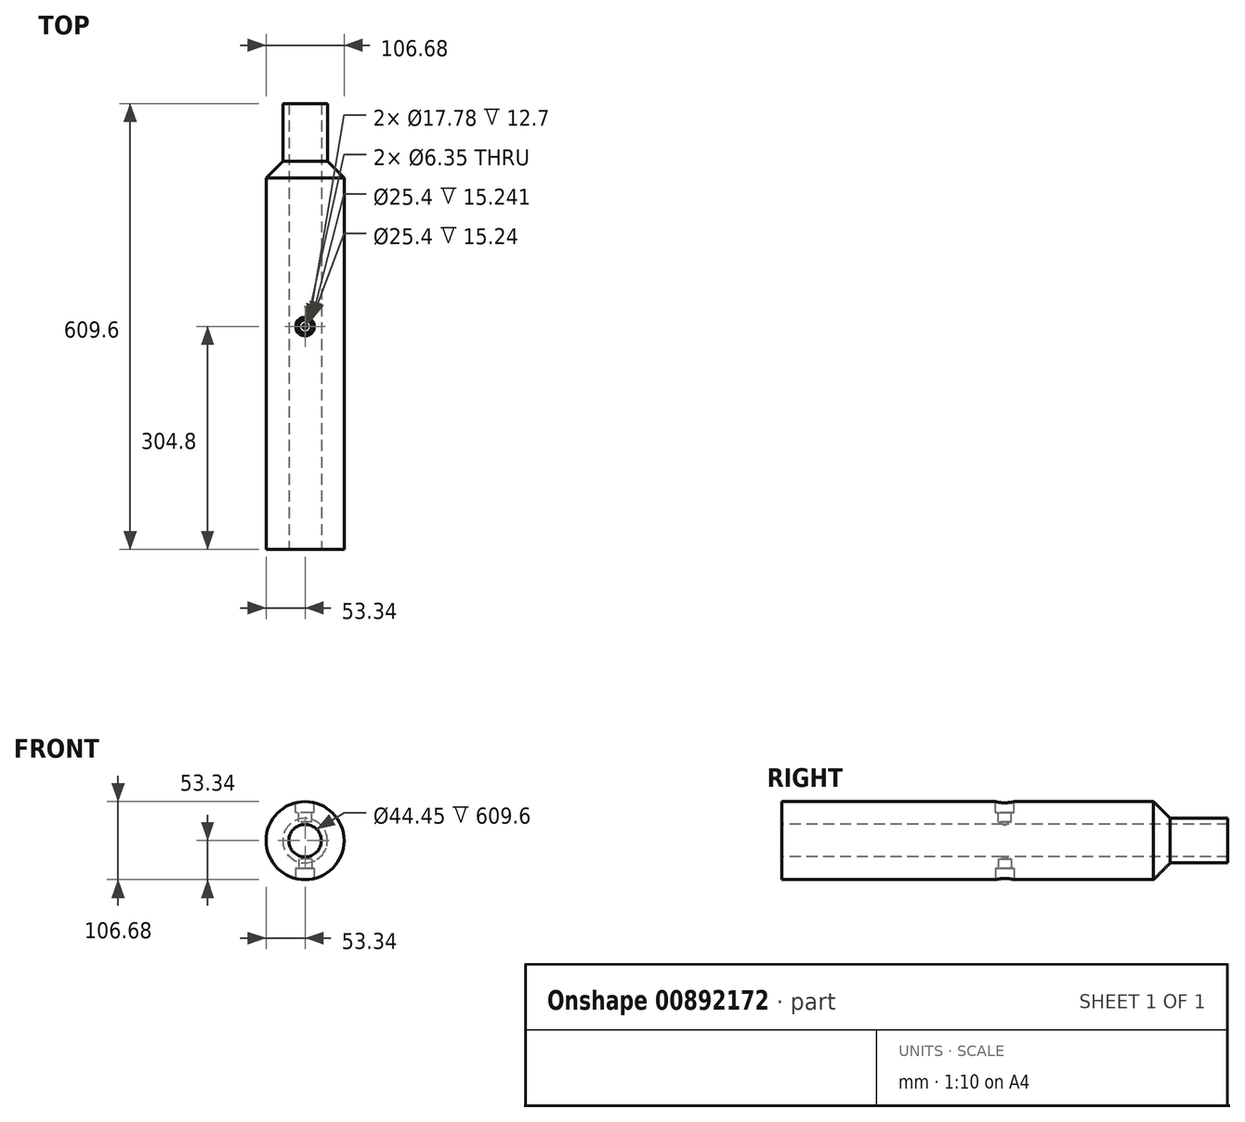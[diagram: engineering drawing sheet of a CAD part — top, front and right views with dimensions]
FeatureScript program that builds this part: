
annotation { "Feature Type Name" : "Feature", "Feature Type Description" : "" }
export const myFeature = defineFeature(function(context is Context, id is Id, definition is map)
    precondition{}
    {
        {
            var Q0;
            Q0=qCreatedBy(makeId("Front.planeOp"),FACE);
            var sketch = newSketch(context, id + "F0", { "sketchPlane" : qUnion([Q0])});
            skCircle(sketch, "E0", {"center": v(0, 0) * mm, "radius": 22.23 * mm});
            skCircle(sketch, "E1", {"center": v(0, 0) * mm, "radius": 53.34 * mm});
            skSolve(sketch);
        }
        {
            var Q0;
            Q0=makeQuery(id+"F0.imprint","IMPRINT",FACE,{"disambiguationData":[TD([[makeQuery(id+"F0.imprint","IMPRINT",EDGE,{"derivedFrom":sQuery(id+"F0.wireOp",EDGE,"E0")}),-1.0]])]});
            extrude(context, id + "F1", {"entities" : qUnion([Q0]), "endBound" : BoundingType.SYMMETRIC, "oppositeDirection" : true, "depth" : 609.6 * mm, "offsetDistance" : 25.4 * mm});
        }
        {
            var Q0;
            Q0=makeQuery(id+"F1.opExtrude","CAP_FACE",FACE,{"disambiguationData":[OSD([sQuery(id+"F0.wireOp",EDGE,"E0"),sQuery(id+"F0.wireOp",EDGE,"E1")])],"isStart":false});
            cPlane(context, id + "F2", {"entities" : qUnion([Q0]), "cplaneType" : CPlaneType.OFFSET, "offset" : 0 * mm, "oppositeDirection" : true, "width" : 152.4 * mm, "height" : 152.4 * mm});
        }
        {
            var Q0;
            Q0=qCreatedBy(makeId("Front.planeOp"),FACE);
            cPlane(context, id + "F3", {"entities" : qUnion([Q0]), "cplaneType" : CPlaneType.OFFSET, "offset" : 203.2 * mm, "oppositeDirection" : true, "width" : 152.4 * mm, "height" : 152.4 * mm});
        }
        {
            var Q0;
            Q0=qCreatedBy(id+"F2.planeOp",FACE);
            var sketch = newSketch(context, id + "F4", { "sketchPlane" : qUnion([Q0])});
            skCircle(sketch, "E2", {"center": v(0, 0) * mm, "radius": 22.23 * mm});
            skCircle(sketch, "E3", {"center": v(0, 0) * mm, "radius": 30.48 * mm});
            skCircle(sketch, "E4", {"center": v(0, 0) * mm, "radius": 53.34 * mm});
            skSolve(sketch);
        }
        {
            var Q0;
            Q0=makeQuery(id+"F4.imprint","IMPRINT",FACE,{"disambiguationData":[TD([[makeQuery(id+"F4.imprint","IMPRINT",EDGE,{"derivedFrom":sQuery(id+"F4.wireOp",EDGE,"E3")}),-1.0]])]});
            var Q1;
            Q1=qCreatedBy(id+"F3.planeOp",FACE);
            extrude(context, id + "F5", {"entities" : qUnion([Q0]), "operationType" : NewBodyOperationType.REMOVE, "oppositeDirection" : true, "depth" : 101.6 * mm, "endBoundEntityFace" : qUnion([Q1]), "offsetDistance" : 25.4 * mm});
        }
        {
            var Q0;
            Q0=qCreatedBy(makeId("Right.planeOp"),FACE);
            var sketch = newSketch(context, id + "F6", { "sketchPlane" : qUnion([Q0])});
            skLineSegment(sketch, "E5", {"start": v(0, 0) * mm, "end": v(203.2, 0) * mm, "construction": true});
            skLineSegment(sketch, "E6", {"start": v(203.2, 0) * mm, "end": v(203.2, 53.34) * mm});
            skLineSegment(sketch, "E7", {"start": v(203.2, 0) * mm, "end": v(203.2, 30.48) * mm});
            skLineSegment(sketch, "E8", {"start": v(203.2, 30.48) * mm, "end": v(226.06, 30.48) * mm});
            skLineSegment(sketch, "E9", {"start": v(226.06, 30.48) * mm, "end": v(203.2, 53.34) * mm});
            skSolve(sketch);
        }
        {
            var Q0;
            Q0=makeQuery(id+"F6.imprint","IMPRINT",FACE,{"disambiguationData":[TD([[makeQuery(id+"F6.imprint","IMPRINT",EDGE,{"derivedFrom":sQuery(id+"F6.wireOp",EDGE,"E6")}),-1.0]])]});
            var Q1;
            Q1=sQuery(id+"F6.wireOp",EDGE,"E5");
            revolve(context, id + "F7", {"operationType" : NewBodyOperationType.ADD, "surfaceOperationType" : NewSurfaceOperationType.NEW, "entities" : qUnion([Q0]), "axis" : qUnion([Q1]), "revolveType" : RevolveType.FULL});
        }
        {
            var Q0;
            Q0=qCreatedBy(makeId("Top.planeOp"),FACE);
            cPlane(context, id + "F8", {"entities" : qUnion([Q0]), "cplaneType" : CPlaneType.OFFSET, "offset" : 53.34 * mm, "width" : 152.4 * mm, "height" : 152.4 * mm});
        }
        {
            var Q0;
            Q0=qCreatedBy(makeId("Top.planeOp"),FACE);
            cPlane(context, id + "F9", {"entities" : qUnion([Q0]), "cplaneType" : CPlaneType.OFFSET, "offset" : 53.34 * mm, "oppositeDirection" : true, "width" : 152.4 * mm, "height" : 152.4 * mm});
        }
        {
            var Q0;
            Q0=qCreatedBy(id+"F8.planeOp",FACE);
            var sketch = newSketch(context, id + "F10", { "sketchPlane" : qUnion([Q0])});
            skCircle(sketch, "E10", {"center": v(0, 0) * mm, "radius": 12.7 * mm});
            skCircle(sketch, "E11", {"center": v(0, 0) * mm, "radius": 8.9 * mm});
            skCircle(sketch, "E12", {"center": v(0, 0) * mm, "radius": 3.18 * mm});
            skSolve(sketch);
        }
        {
            var Q0;
            Q0=makeQuery(id+"F10.imprint","IMPRINT",FACE,{"disambiguationData":[TD([[makeQuery(id+"F10.imprint","IMPRINT",EDGE,{"derivedFrom":sQuery(id+"F10.wireOp",EDGE,"E10")}),1.0]])]});
            var Q1;
            Q1=makeQuery(id+"F10.imprint","IMPRINT",FACE,{"disambiguationData":[TD([[makeQuery(id+"F10.imprint","IMPRINT",EDGE,{"derivedFrom":sQuery(id+"F10.wireOp",EDGE,"E12")}),1.0]])]});
            var Q2;
            Q2=makeQuery(id+"F10.imprint","IMPRINT",FACE,{"disambiguationData":[TD([[makeQuery(id+"F10.imprint","IMPRINT",EDGE,{"derivedFrom":sQuery(id+"F10.wireOp",EDGE,"E11")}),1.0]])]});
            extrude(context, id + "F11", {"entities" : qUnion([Q0, Q1, Q2]), "operationType" : NewBodyOperationType.REMOVE, "oppositeDirection" : true, "depth" : 15.24 * mm, "offsetDistance" : 25.4 * mm});
        }
        {
            var Q0;
            Q0=makeQuery(id+"F10.imprint","IMPRINT",FACE,{"disambiguationData":[TD([[makeQuery(id+"F10.imprint","IMPRINT",EDGE,{"derivedFrom":sQuery(id+"F10.wireOp",EDGE,"E11")}),1.0]])]});
            var Q1;
            Q1=makeQuery(id+"F10.imprint","IMPRINT",FACE,{"disambiguationData":[TD([[makeQuery(id+"F10.imprint","IMPRINT",EDGE,{"derivedFrom":sQuery(id+"F10.wireOp",EDGE,"E12")}),1.0]])]});
            extrude(context, id + "F12", {"entities" : qUnion([Q0, Q1]), "operationType" : NewBodyOperationType.REMOVE, "oppositeDirection" : true, "depth" : 27.94 * mm, "offsetDistance" : 25.4 * mm});
        }
        {
            var Q0;
            Q0=makeQuery(id+"F10.imprint","IMPRINT",FACE,{"disambiguationData":[TD([[makeQuery(id+"F10.imprint","IMPRINT",EDGE,{"derivedFrom":sQuery(id+"F10.wireOp",EDGE,"E12")}),1.0]])]});
            var Q1;
            Q1=makeQuery(id+"F1.opExtrude","SWEPT_FACE",FACE,{"disambiguationData":[OSD([sQuery(id+"F0.wireOp",EDGE,"E0")])]});
            extrude(context, id + "F13", {"entities" : qUnion([Q0]), "operationType" : NewBodyOperationType.REMOVE, "endBound" : BoundingType.UP_TO_SURFACE, "oppositeDirection" : true, "depth" : 53.34 * mm, "endBoundEntityFace" : qUnion([Q1]), "offsetDistance" : 25.4 * mm});
        }
        {
            var Q0;
            Q0=qCreatedBy(id+"F9.planeOp",FACE);
            var sketch = newSketch(context, id + "F14", { "sketchPlane" : qUnion([Q0])});
            skCircle(sketch, "E13", {"center": v(0, 0) * mm, "radius": 12.7 * mm});
            skCircle(sketch, "E14", {"center": v(0, 0) * mm, "radius": 8.9 * mm});
            skCircle(sketch, "E15", {"center": v(0, 0) * mm, "radius": 3.18 * mm});
            skSolve(sketch);
        }
        {
            var Q0;
            Q0 = qSketchRegion(id + "F14", true);
            var Q1;
            Q1=makeQuery(id+"F14.imprint","IMPRINT",FACE,{"disambiguationData":[TD([[makeQuery(id+"F14.imprint","IMPRINT",EDGE,{"derivedFrom":sQuery(id+"F14.wireOp",EDGE,"E14")}),1.0]])]});
            var Q2;
            Q2=makeQuery(id+"F14.imprint","IMPRINT",FACE,{"disambiguationData":[TD([[makeQuery(id+"F14.imprint","IMPRINT",EDGE,{"derivedFrom":sQuery(id+"F14.wireOp",EDGE,"E15")}),1.0]])]});
            extrude(context, id + "F15", {"entities" : qUnion([Q0, Q1, Q2]), "operationType" : NewBodyOperationType.REMOVE, "depth" : 15.24 * mm, "offsetDistance" : 25.4 * mm});
        }
        {
            var Q0;
            Q0=makeQuery(id+"F14.imprint","IMPRINT",FACE,{"disambiguationData":[TD([[makeQuery(id+"F14.imprint","IMPRINT",EDGE,{"derivedFrom":sQuery(id+"F14.wireOp",EDGE,"E14")}),1.0]])]});
            var Q1;
            Q1=makeQuery(id+"F14.imprint","IMPRINT",FACE,{"disambiguationData":[TD([[makeQuery(id+"F14.imprint","IMPRINT",EDGE,{"derivedFrom":sQuery(id+"F14.wireOp",EDGE,"E15")}),1.0]])]});
            extrude(context, id + "F16", {"entities" : qUnion([Q0, Q1]), "operationType" : NewBodyOperationType.REMOVE, "depth" : 27.94 * mm, "offsetDistance" : 25.4 * mm});
        }
        {
            var Q0;
            Q0=makeQuery(id+"F14.imprint","IMPRINT",FACE,{"disambiguationData":[TD([[makeQuery(id+"F14.imprint","IMPRINT",EDGE,{"derivedFrom":sQuery(id+"F14.wireOp",EDGE,"E15")}),1.0]])]});
            var Q1;
            Q1=makeQuery(id+"F1.opExtrude","SWEPT_FACE",FACE,{"disambiguationData":[OSD([sQuery(id+"F0.wireOp",EDGE,"E0")])]});
            extrude(context, id + "F17", {"entities" : qUnion([Q0]), "operationType" : NewBodyOperationType.REMOVE, "endBound" : BoundingType.UP_TO_SURFACE, "depth" : 25.4 * mm, "endBoundEntityFace" : qUnion([Q1]), "offsetDistance" : 25.4 * mm});
        }
    });
